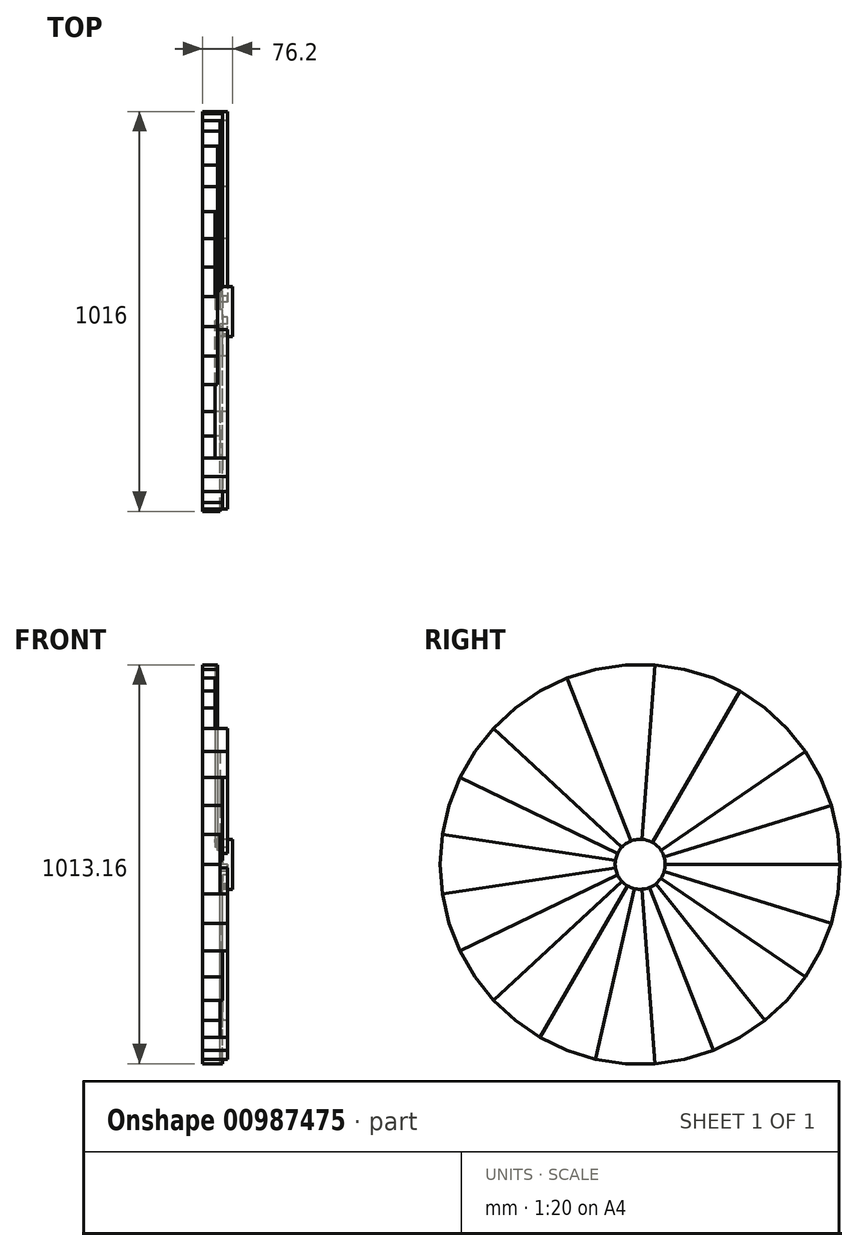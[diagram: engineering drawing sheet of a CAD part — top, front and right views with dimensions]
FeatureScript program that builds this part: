
annotation { "Feature Type Name" : "Feature", "Feature Type Description" : "" }
export const myFeature = defineFeature(function(context is Context, id is Id, definition is map)
    precondition{}
    {
        {
            var Q0;
            Q0=qCreatedBy(makeId("Right.planeOp"),FACE);
            var sketch = newSketch(context, id + "F0", { "sketchPlane" : qUnion([Q0])});
            skCircle(sketch, "E0", {"center": v(0, 0) * mm, "radius": 508 * mm});
            skCircle(sketch, "E1.cCircle", {"center": v(0, 0) * mm, "radius": 508 * mm, "construction": true});
            skLineSegment(sketch, "E1.0", {"start": v(-185.6, 472.88) * mm, "end": v(-113.04, 495.26) * mm});
            skLineSegment(sketch, "E1.1", {"start": v(-113.04, 495.26) * mm, "end": v(-37.96, 506.58) * mm});
            skLineSegment(sketch, "E1.2", {"start": v(-37.96, 506.58) * mm, "end": v(37.96, 506.58) * mm});
            skLineSegment(sketch, "E1.3", {"start": v(37.96, 506.58) * mm, "end": v(113.04, 495.26) * mm});
            skLineSegment(sketch, "E1.4", {"start": v(113.04, 495.26) * mm, "end": v(185.6, 472.88) * mm});
            skLineSegment(sketch, "E1.5", {"start": v(185.6, 472.88) * mm, "end": v(254, 439.94) * mm});
            skLineSegment(sketch, "E1.6", {"start": v(254, 439.94) * mm, "end": v(316.73, 397.17) * mm});
            skLineSegment(sketch, "E1.7", {"start": v(316.73, 397.17) * mm, "end": v(372.4, 345.53) * mm});
            skLineSegment(sketch, "E1.8", {"start": v(372.4, 345.53) * mm, "end": v(419.73, 286.17) * mm});
            skLineSegment(sketch, "E1.9", {"start": v(419.73, 286.17) * mm, "end": v(457.7, 220.41) * mm});
            skLineSegment(sketch, "E1.10", {"start": v(457.7, 220.41) * mm, "end": v(485.43, 149.74) * mm});
            skLineSegment(sketch, "E1.11", {"start": v(485.43, 149.74) * mm, "end": v(502.33, 75.71) * mm});
            skLineSegment(sketch, "E1.12", {"start": v(502.33, 75.71) * mm, "end": v(508, 0) * mm});
            skLineSegment(sketch, "E1.13", {"start": v(508, 0) * mm, "end": v(502.33, -75.71) * mm});
            skLineSegment(sketch, "E1.14", {"start": v(502.33, -75.71) * mm, "end": v(485.43, -149.74) * mm});
            skLineSegment(sketch, "E1.15", {"start": v(485.43, -149.74) * mm, "end": v(457.7, -220.41) * mm});
            skLineSegment(sketch, "E1.16", {"start": v(457.7, -220.41) * mm, "end": v(419.73, -286.17) * mm});
            skLineSegment(sketch, "E1.17", {"start": v(419.73, -286.17) * mm, "end": v(372.4, -345.53) * mm});
            skLineSegment(sketch, "E1.18", {"start": v(372.4, -345.53) * mm, "end": v(316.73, -397.17) * mm});
            skLineSegment(sketch, "E1.19", {"start": v(316.73, -397.17) * mm, "end": v(254, -439.94) * mm});
            skLineSegment(sketch, "E1.20", {"start": v(254, -439.94) * mm, "end": v(185.6, -472.88) * mm});
            skLineSegment(sketch, "E1.21", {"start": v(185.6, -472.88) * mm, "end": v(113.04, -495.26) * mm});
            skLineSegment(sketch, "E1.22", {"start": v(113.04, -495.26) * mm, "end": v(37.96, -506.58) * mm});
            skLineSegment(sketch, "E1.23", {"start": v(37.96, -506.58) * mm, "end": v(-37.96, -506.58) * mm});
            skLineSegment(sketch, "E1.24", {"start": v(-37.96, -506.58) * mm, "end": v(-113.04, -495.26) * mm});
            skLineSegment(sketch, "E1.25", {"start": v(-113.04, -495.26) * mm, "end": v(-185.6, -472.88) * mm});
            skLineSegment(sketch, "E1.26", {"start": v(-185.6, -472.88) * mm, "end": v(-254, -439.94) * mm});
            skLineSegment(sketch, "E1.27", {"start": v(-254, -439.94) * mm, "end": v(-316.73, -397.17) * mm});
            skLineSegment(sketch, "E1.28", {"start": v(-316.73, -397.17) * mm, "end": v(-372.4, -345.53) * mm});
            skLineSegment(sketch, "E1.29", {"start": v(-372.4, -345.53) * mm, "end": v(-419.73, -286.17) * mm});
            skLineSegment(sketch, "E1.30", {"start": v(-419.73, -286.17) * mm, "end": v(-457.7, -220.41) * mm});
            skLineSegment(sketch, "E1.31", {"start": v(-457.7, -220.41) * mm, "end": v(-485.43, -149.74) * mm});
            skLineSegment(sketch, "E1.32", {"start": v(-485.43, -149.74) * mm, "end": v(-502.33, -75.71) * mm});
            skLineSegment(sketch, "E1.33", {"start": v(-502.33, -75.71) * mm, "end": v(-508, 0) * mm});
            skLineSegment(sketch, "E1.34", {"start": v(-508, 0) * mm, "end": v(-502.33, 75.71) * mm});
            skLineSegment(sketch, "E1.35", {"start": v(-502.33, 75.71) * mm, "end": v(-485.43, 149.74) * mm});
            skLineSegment(sketch, "E1.36", {"start": v(-485.43, 149.74) * mm, "end": v(-457.7, 220.41) * mm});
            skLineSegment(sketch, "E1.37", {"start": v(-457.7, 220.41) * mm, "end": v(-419.73, 286.17) * mm});
            skLineSegment(sketch, "E1.38", {"start": v(-419.73, 286.17) * mm, "end": v(-372.4, 345.53) * mm});
            skLineSegment(sketch, "E1.39", {"start": v(-372.4, 345.53) * mm, "end": v(-316.73, 397.17) * mm});
            skLineSegment(sketch, "E1.40", {"start": v(-316.73, 397.17) * mm, "end": v(-254, 439.94) * mm});
            skLineSegment(sketch, "E1.41", {"start": v(-254, 439.94) * mm, "end": v(-185.6, 472.88) * mm});
            skLineSegment(sketch, "E2", {"start": v(37.96, 506.58) * mm, "end": v(0, 0) * mm});
            skLineSegment(sketch, "E3", {"start": v(254, 439.94) * mm, "end": v(0, 0) * mm});
            skLineSegment(sketch, "E4", {"start": v(419.73, 286.17) * mm, "end": v(0, 0) * mm});
            skLineSegment(sketch, "E5", {"start": v(-185.6, 472.88) * mm, "end": v(0, 0) * mm});
            skLineSegment(sketch, "E6", {"start": v(-372.4, 345.53) * mm, "end": v(0, 0) * mm});
            skLineSegment(sketch, "E7", {"start": v(485.43, 149.74) * mm, "end": v(0, 0) * mm});
            skLineSegment(sketch, "E8", {"start": v(508, 0) * mm, "end": v(0, 0) * mm});
            skLineSegment(sketch, "E9", {"start": v(485.43, -149.74) * mm, "end": v(0, 0) * mm});
            skLineSegment(sketch, "E10", {"start": v(419.73, -286.17) * mm, "end": v(0, 0) * mm});
            skLineSegment(sketch, "E11", {"start": v(316.73, -397.17) * mm, "end": v(0, 0) * mm});
            skLineSegment(sketch, "E12", {"start": v(185.6, -472.88) * mm, "end": v(0, 0) * mm});
            skLineSegment(sketch, "E13", {"start": v(37.96, -506.58) * mm, "end": v(0, 0) * mm});
            skLineSegment(sketch, "E14", {"start": v(-113.04, -495.26) * mm, "end": v(0, 0) * mm});
            skLineSegment(sketch, "E15", {"start": v(-254, -439.94) * mm, "end": v(0, 0) * mm});
            skLineSegment(sketch, "E16", {"start": v(-372.4, -345.53) * mm, "end": v(0, 0) * mm});
            skLineSegment(sketch, "E17", {"start": v(-457.7, -220.41) * mm, "end": v(0, 0) * mm});
            skLineSegment(sketch, "E18", {"start": v(-502.33, -75.71) * mm, "end": v(0, 0) * mm});
            skLineSegment(sketch, "E19", {"start": v(-502.33, 75.71) * mm, "end": v(0, 0) * mm});
            skLineSegment(sketch, "E20", {"start": v(-457.7, 220.41) * mm, "end": v(0, 0) * mm});
            skCircle(sketch, "E21", {"center": v(1271.03, -28.32) * mm, "radius": 508 * mm});
            skCircle(sketch, "E22", {"center": v(-1617.24, 20.06) * mm, "radius": 508 * mm});
            skCircle(sketch, "E23.cCircle", {"center": v(-1617.24, 20.06) * mm, "radius": 508 * mm, "construction": true});
            skLineSegment(sketch, "E23.0", {"start": v(-1897.2, 443.96) * mm, "end": v(-1830.9, 480.95) * mm});
            skLineSegment(sketch, "E23.1", {"start": v(-1830.9, 480.95) * mm, "end": v(-1759.81, 507.65) * mm});
            skLineSegment(sketch, "E23.2", {"start": v(-1759.81, 507.65) * mm, "end": v(-1685.55, 523.45) * mm});
            skLineSegment(sketch, "E23.3", {"start": v(-1685.55, 523.45) * mm, "end": v(-1609.76, 528) * mm});
            skLineSegment(sketch, "E23.4", {"start": v(-1609.76, 528) * mm, "end": v(-1534.14, 521.22) * mm});
            skLineSegment(sketch, "E23.5", {"start": v(-1534.14, 521.22) * mm, "end": v(-1460.37, 503.23) * mm});
            skLineSegment(sketch, "E23.6", {"start": v(-1460.37, 503.23) * mm, "end": v(-1390.11, 474.46) * mm});
            skLineSegment(sketch, "E23.7", {"start": v(-1390.11, 474.46) * mm, "end": v(-1324.93, 435.53) * mm});
            skLineSegment(sketch, "E23.8", {"start": v(-1324.93, 435.53) * mm, "end": v(-1266.27, 387.32) * mm});
            skLineSegment(sketch, "E23.9", {"start": v(-1266.27, 387.32) * mm, "end": v(-1215.45, 330.9) * mm});
            skLineSegment(sketch, "E23.10", {"start": v(-1215.45, 330.9) * mm, "end": v(-1173.6, 267.55) * mm});
            skLineSegment(sketch, "E23.11", {"start": v(-1173.6, 267.55) * mm, "end": v(-1141.68, 198.67) * mm});
            skLineSegment(sketch, "E23.12", {"start": v(-1141.68, 198.67) * mm, "end": v(-1120.37, 125.8) * mm});
            skLineSegment(sketch, "E23.13", {"start": v(-1120.37, 125.8) * mm, "end": v(-1110.16, 50.56) * mm});
            skLineSegment(sketch, "E23.14", {"start": v(-1110.16, 50.56) * mm, "end": v(-1111.28, -25.36) * mm});
            skLineSegment(sketch, "E23.15", {"start": v(-1111.28, -25.36) * mm, "end": v(-1123.7, -100.26) * mm});
            skLineSegment(sketch, "E23.16", {"start": v(-1123.7, -100.26) * mm, "end": v(-1147.15, -172.48) * mm});
            skLineSegment(sketch, "E23.17", {"start": v(-1147.15, -172.48) * mm, "end": v(-1181.1, -240.4) * mm});
            skLineSegment(sketch, "E23.18", {"start": v(-1181.1, -240.4) * mm, "end": v(-1224.78, -302.49) * mm});
            skLineSegment(sketch, "E23.19", {"start": v(-1224.78, -302.49) * mm, "end": v(-1277.24, -357.38) * mm});
            skLineSegment(sketch, "E23.20", {"start": v(-1277.24, -357.38) * mm, "end": v(-1337.3, -403.84) * mm});
            skLineSegment(sketch, "E23.21", {"start": v(-1337.3, -403.84) * mm, "end": v(-1403.6, -440.83) * mm});
            skLineSegment(sketch, "E23.22", {"start": v(-1403.6, -440.83) * mm, "end": v(-1474.68, -467.52) * mm});
            skLineSegment(sketch, "E23.23", {"start": v(-1474.68, -467.52) * mm, "end": v(-1548.94, -483.33) * mm});
            skLineSegment(sketch, "E23.24", {"start": v(-1548.94, -483.33) * mm, "end": v(-1624.73, -487.88) * mm});
            skLineSegment(sketch, "E23.25", {"start": v(-1624.73, -487.88) * mm, "end": v(-1700.35, -481.1) * mm});
            skLineSegment(sketch, "E23.26", {"start": v(-1700.35, -481.1) * mm, "end": v(-1774.11, -463.11) * mm});
            skLineSegment(sketch, "E23.27", {"start": v(-1774.11, -463.11) * mm, "end": v(-1844.38, -434.33) * mm});
            skLineSegment(sketch, "E23.28", {"start": v(-1844.38, -434.33) * mm, "end": v(-1909.56, -395.4) * mm});
            skLineSegment(sketch, "E23.29", {"start": v(-1909.56, -395.4) * mm, "end": v(-1968.22, -347.2) * mm});
            skLineSegment(sketch, "E23.30", {"start": v(-1968.22, -347.2) * mm, "end": v(-2019.04, -290.79) * mm});
            skLineSegment(sketch, "E23.31", {"start": v(-2019.04, -290.79) * mm, "end": v(-2060.88, -227.43) * mm});
            skLineSegment(sketch, "E23.32", {"start": v(-2060.88, -227.43) * mm, "end": v(-2092.81, -158.55) * mm});
            skLineSegment(sketch, "E23.33", {"start": v(-2092.81, -158.55) * mm, "end": v(-2114.12, -85.67) * mm});
            skLineSegment(sketch, "E23.34", {"start": v(-2114.12, -85.67) * mm, "end": v(-2124.33, -10.43) * mm});
            skLineSegment(sketch, "E23.35", {"start": v(-2124.33, -10.43) * mm, "end": v(-2123.2, 65.48) * mm});
            skLineSegment(sketch, "E23.36", {"start": v(-2123.2, 65.48) * mm, "end": v(-2110.79, 140.39) * mm});
            skLineSegment(sketch, "E23.37", {"start": v(-2110.79, 140.39) * mm, "end": v(-2087.34, 212.6) * mm});
            skLineSegment(sketch, "E23.38", {"start": v(-2087.34, 212.6) * mm, "end": v(-2053.4, 280.51) * mm});
            skLineSegment(sketch, "E23.39", {"start": v(-2053.4, 280.51) * mm, "end": v(-2009.7, 342.61) * mm});
            skLineSegment(sketch, "E23.40", {"start": v(-2009.7, 342.61) * mm, "end": v(-1957.25, 397.5) * mm});
            skLineSegment(sketch, "E23.41", {"start": v(-1957.25, 397.5) * mm, "end": v(-1897.2, 443.96) * mm});
            skLineSegment(sketch, "E24", {"start": v(-1685.55, 523.45) * mm, "end": v(-1617.24, 20.06) * mm});
            skLineSegment(sketch, "E25", {"start": v(-1460.37, 503.23) * mm, "end": v(-1617.24, 20.06) * mm});
            skLineSegment(sketch, "E26", {"start": v(-1266.27, 387.32) * mm, "end": v(-1617.24, 20.06) * mm});
            skLineSegment(sketch, "E27", {"start": v(-1897.2, 443.96) * mm, "end": v(-1617.24, 20.06) * mm});
            skLineSegment(sketch, "E28", {"start": v(-2053.4, 280.51) * mm, "end": v(-1617.24, 20.06) * mm});
            skLineSegment(sketch, "E29", {"start": v(-1173.6, 267.55) * mm, "end": v(-1617.24, 20.06) * mm});
            skLineSegment(sketch, "E30", {"start": v(-1120.37, 125.8) * mm, "end": v(-1617.24, 20.06) * mm});
            skLineSegment(sketch, "E31", {"start": v(-1111.28, -25.36) * mm, "end": v(-1617.24, 20.06) * mm});
            skLineSegment(sketch, "E32", {"start": v(-1147.15, -172.48) * mm, "end": v(-1617.24, 20.06) * mm});
            skLineSegment(sketch, "E33", {"start": v(-1224.78, -302.49) * mm, "end": v(-1617.24, 20.06) * mm});
            skLineSegment(sketch, "E34", {"start": v(-1337.3, -403.84) * mm, "end": v(-1617.24, 20.06) * mm});
            skLineSegment(sketch, "E35", {"start": v(-1474.68, -467.52) * mm, "end": v(-1617.24, 20.06) * mm});
            skLineSegment(sketch, "E36", {"start": v(-1624.73, -487.88) * mm, "end": v(-1617.24, 20.06) * mm});
            skLineSegment(sketch, "E37", {"start": v(-1774.11, -463.11) * mm, "end": v(-1617.24, 20.06) * mm});
            skLineSegment(sketch, "E38", {"start": v(-1909.56, -395.4) * mm, "end": v(-1617.24, 20.06) * mm});
            skLineSegment(sketch, "E39", {"start": v(-2019.04, -290.79) * mm, "end": v(-1617.24, 20.06) * mm});
            skLineSegment(sketch, "E40", {"start": v(-2092.81, -158.55) * mm, "end": v(-1617.24, 20.06) * mm});
            skLineSegment(sketch, "E41", {"start": v(-2124.33, -10.43) * mm, "end": v(-1617.24, 20.06) * mm});
            skLineSegment(sketch, "E42", {"start": v(-2110.79, 140.39) * mm, "end": v(-1617.24, 20.06) * mm});
            skCircle(sketch, "E43", {"center": v(0, 0) * mm, "radius": 63.5 * mm});
            skLineSegment(sketch, "E44", {"start": v(0, 0) * mm, "end": v(0, 508) * mm, "construction": true});
            skSolve(sketch);
        }
        {
            var Q0;
            Q0=makeQuery(id+"F0.imprint","IMPRINT",FACE,{"disambiguationData":[TD([[makeQuery(id+"F0.imprint","IMPRINT",EDGE,{"derivedFrom":sQuery(id+"F0.wireOp",EDGE,"E1.0")}),-1.0]])]});
            var Q1;
            Q1=makeQuery(id+"F0.imprint","IMPRINT",FACE,{"disambiguationData":[TD([[makeQuery(id+"F0.imprint","IMPRINT",EDGE,{"derivedFrom":sQuery(id+"F0.wireOp",EDGE,"E1.3")}),-1.0]])]});
            var Q2;
            Q2=makeQuery(id+"F0.imprint","IMPRINT",FACE,{"disambiguationData":[TD([[makeQuery(id+"F0.imprint","IMPRINT",EDGE,{"derivedFrom":sQuery(id+"F0.wireOp",EDGE,"E1.6")}),-1.0]])]});
            var Q3;
            Q3=makeQuery(id+"F0.imprint","IMPRINT",FACE,{"disambiguationData":[TD([[makeQuery(id+"F0.imprint","IMPRINT",EDGE,{"derivedFrom":sQuery(id+"F0.wireOp",EDGE,"E1.9")}),-1.0]])]});
            var Q4;
            Q4=makeQuery(id+"F0.imprint","IMPRINT",FACE,{"disambiguationData":[TD([[makeQuery(id+"F0.imprint","IMPRINT",EDGE,{"derivedFrom":sQuery(id+"F0.wireOp",EDGE,"E1.11")}),-1.0]])]});
            var Q5;
            Q5=makeQuery(id+"F0.imprint","IMPRINT",FACE,{"disambiguationData":[TD([[makeQuery(id+"F0.imprint","IMPRINT",EDGE,{"derivedFrom":sQuery(id+"F0.wireOp",EDGE,"E1.13")}),-1.0]])]});
            var Q6;
            Q6=makeQuery(id+"F0.imprint","IMPRINT",FACE,{"disambiguationData":[TD([[makeQuery(id+"F0.imprint","IMPRINT",EDGE,{"derivedFrom":sQuery(id+"F0.wireOp",EDGE,"E1.15")}),-1.0]])]});
            var Q7;
            Q7=makeQuery(id+"F0.imprint","IMPRINT",FACE,{"disambiguationData":[TD([[makeQuery(id+"F0.imprint","IMPRINT",EDGE,{"derivedFrom":sQuery(id+"F0.wireOp",EDGE,"E1.17")}),-1.0]])]});
            var Q8;
            Q8=makeQuery(id+"F0.imprint","IMPRINT",FACE,{"disambiguationData":[TD([[makeQuery(id+"F0.imprint","IMPRINT",EDGE,{"derivedFrom":sQuery(id+"F0.wireOp",EDGE,"E1.19")}),-1.0]])]});
            var Q9;
            Q9=makeQuery(id+"F0.imprint","IMPRINT",FACE,{"disambiguationData":[TD([[makeQuery(id+"F0.imprint","IMPRINT",EDGE,{"derivedFrom":sQuery(id+"F0.wireOp",EDGE,"E1.21")}),-1.0]])]});
            var Q10;
            Q10=makeQuery(id+"F0.imprint","IMPRINT",FACE,{"disambiguationData":[TD([[makeQuery(id+"F0.imprint","IMPRINT",EDGE,{"derivedFrom":sQuery(id+"F0.wireOp",EDGE,"E1.23")}),-1.0]])]});
            var Q11;
            Q11=makeQuery(id+"F0.imprint","IMPRINT",FACE,{"disambiguationData":[TD([[makeQuery(id+"F0.imprint","IMPRINT",EDGE,{"derivedFrom":sQuery(id+"F0.wireOp",EDGE,"E1.25")}),-1.0]])]});
            var Q12;
            Q12=makeQuery(id+"F0.imprint","IMPRINT",FACE,{"disambiguationData":[TD([[makeQuery(id+"F0.imprint","IMPRINT",EDGE,{"derivedFrom":sQuery(id+"F0.wireOp",EDGE,"E1.27")}),-1.0]])]});
            var Q13;
            Q13=makeQuery(id+"F0.imprint","IMPRINT",FACE,{"disambiguationData":[TD([[makeQuery(id+"F0.imprint","IMPRINT",EDGE,{"derivedFrom":sQuery(id+"F0.wireOp",EDGE,"E1.29")}),-1.0]])]});
            var Q14;
            Q14=makeQuery(id+"F0.imprint","IMPRINT",FACE,{"disambiguationData":[TD([[makeQuery(id+"F0.imprint","IMPRINT",EDGE,{"derivedFrom":sQuery(id+"F0.wireOp",EDGE,"E1.31")}),-1.0]])]});
            var Q15;
            Q15=makeQuery(id+"F0.imprint","IMPRINT",FACE,{"disambiguationData":[TD([[makeQuery(id+"F0.imprint","IMPRINT",EDGE,{"derivedFrom":sQuery(id+"F0.wireOp",EDGE,"E1.33")}),-1.0]])]});
            var Q16;
            Q16=makeQuery(id+"F0.imprint","IMPRINT",FACE,{"disambiguationData":[TD([[makeQuery(id+"F0.imprint","IMPRINT",EDGE,{"derivedFrom":sQuery(id+"F0.wireOp",EDGE,"E1.35")}),-1.0]])]});
            var Q17;
            Q17=makeQuery(id+"F0.imprint","IMPRINT",FACE,{"disambiguationData":[TD([[makeQuery(id+"F0.imprint","IMPRINT",EDGE,{"derivedFrom":sQuery(id+"F0.wireOp",EDGE,"E1.37")}),-1.0]])]});
            var Q18;
            Q18=makeQuery(id+"F0.imprint","IMPRINT",FACE,{"disambiguationData":[TD([[makeQuery(id+"F0.imprint","IMPRINT",EDGE,{"derivedFrom":sQuery(id+"F0.wireOp",EDGE,"E1.39")}),-1.0]])]});
            extrude(context, id + "F1", {"entities" : qUnion([Q0, Q1, Q2, Q3, Q4, Q5, Q6, Q7, Q8, Q9, Q10, Q11, Q12, Q13, Q14, Q15, Q16, Q17, Q18]), "depth" : 25.4 * mm, "offsetDistance" : 25.4 * mm});
        }
        {
            var Q0;
            {var subQ1=sQuery(id+"F0.wireOp",EDGE,"E1.3");Q0=makeQuery(id+"F0.imprint","IMPRINT",FACE,{"disambiguationData":[TD([[makeQuery(id+"F0.imprint","IMPRINT",EDGE,{"derivedFrom":subQ1}),-1.0]])]});}
            var Q1;
            {var subQ5=sQuery(id+"F0.wireOp",EDGE,"E1.39");Q1=makeQuery(id+"F0.imprint","IMPRINT",FACE,{"disambiguationData":[TD([[makeQuery(id+"F0.imprint","IMPRINT",EDGE,{"derivedFrom":subQ5}),-1.0]])]});}
            var Q2;
            {var subQ1=sQuery(id+"F0.wireOp",EDGE,"E2");var subQ3=sQuery(id+"F0.wireOp",EDGE,"E43");var subQ4=makeQuery(id+"F0.imprint","INTERSECT",VERTEX,{"derivedFrom":[subQ1,subQ3]});Q2=makeQuery(id+"F0.imprint","IMPRINT",FACE,{"disambiguationData":[TD([[makeQuery(id+"F0.imprint","IMPRINT",EDGE,{"disambiguationData":[TD([[subQ4,1.0]])],"derivedFrom":subQ3}),1.0]])]});}
            var Q3;
            {var subQ1=sQuery(id+"F0.wireOp",EDGE,"E2");var subQ3=sQuery(id+"F0.wireOp",EDGE,"E43");var subQ4=makeQuery(id+"F0.imprint","INTERSECT",VERTEX,{"derivedFrom":[subQ1,subQ3]});Q3=makeQuery(id+"F0.imprint","IMPRINT",FACE,{"disambiguationData":[TD([[makeQuery(id+"F0.imprint","IMPRINT",EDGE,{"disambiguationData":[TD([[subQ4,-1.0]])],"derivedFrom":subQ3}),1.0]])]});}
            var Q4;
            {var subQ1=sQuery(id+"F0.wireOp",EDGE,"E5");var subQ3=sQuery(id+"F0.wireOp",EDGE,"E43");var subQ4=makeQuery(id+"F0.imprint","INTERSECT",VERTEX,{"derivedFrom":[subQ1,subQ3]});Q4=makeQuery(id+"F0.imprint","IMPRINT",FACE,{"disambiguationData":[TD([[makeQuery(id+"F0.imprint","IMPRINT",EDGE,{"disambiguationData":[TD([[subQ4,-1.0]])],"derivedFrom":subQ3}),1.0]])]});}
            extrude(context, id + "F2", {"entities" : qUnion([Q0, Q1, Q2, Q3, Q4]), "operationType" : NewBodyOperationType.ADD, "depth" : 31.75 * mm, "offsetDistance" : 25.4 * mm});
        }
        {
            var Q0;
            {var subQ7=sQuery(id+"F0.wireOp",EDGE,"E1.0");Q0=makeQuery(id+"F0.imprint","IMPRINT",FACE,{"disambiguationData":[TD([[makeQuery(id+"F0.imprint","IMPRINT",EDGE,{"derivedFrom":subQ7}),-1.0]])]});}
            var Q1;
            {var subQ1=sQuery(id+"F0.wireOp",EDGE,"E1.6");Q1=makeQuery(id+"F0.imprint","IMPRINT",FACE,{"disambiguationData":[TD([[makeQuery(id+"F0.imprint","IMPRINT",EDGE,{"derivedFrom":subQ1}),-1.0]])]});}
            var Q2;
            {var subQ1=sQuery(id+"F0.wireOp",EDGE,"E3");var subQ3=sQuery(id+"F0.wireOp",EDGE,"E43");var subQ4=makeQuery(id+"F0.imprint","INTERSECT",VERTEX,{"derivedFrom":[subQ1,subQ3]});Q2=makeQuery(id+"F0.imprint","IMPRINT",FACE,{"disambiguationData":[TD([[makeQuery(id+"F0.imprint","IMPRINT",EDGE,{"disambiguationData":[TD([[subQ4,1.0]])],"derivedFrom":subQ3}),1.0]])]});}
            var Q3;
            {var subQ1=sQuery(id+"F0.wireOp",EDGE,"E2");var subQ3=sQuery(id+"F0.wireOp",EDGE,"E43");var subQ4=makeQuery(id+"F0.imprint","INTERSECT",VERTEX,{"derivedFrom":[subQ1,subQ3]});Q3=makeQuery(id+"F0.imprint","IMPRINT",FACE,{"disambiguationData":[TD([[makeQuery(id+"F0.imprint","IMPRINT",EDGE,{"disambiguationData":[TD([[subQ4,1.0]])],"derivedFrom":subQ3}),1.0]])]});}
            var Q4;
            {var subQ1=sQuery(id+"F0.wireOp",EDGE,"E2");var subQ3=sQuery(id+"F0.wireOp",EDGE,"E43");var subQ4=makeQuery(id+"F0.imprint","INTERSECT",VERTEX,{"derivedFrom":[subQ1,subQ3]});Q4=makeQuery(id+"F0.imprint","IMPRINT",FACE,{"disambiguationData":[TD([[makeQuery(id+"F0.imprint","IMPRINT",EDGE,{"disambiguationData":[TD([[subQ4,-1.0]])],"derivedFrom":subQ3}),1.0]])]});}
            extrude(context, id + "F3", {"entities" : qUnion([Q0, Q1, Q2, Q3, Q4]), "operationType" : NewBodyOperationType.ADD, "depth" : 38.1 * mm, "offsetDistance" : 25.4 * mm});
        }
        {
            var Q0;
            {var subQ6=sQuery(id+"F0.wireOp",EDGE,"E1.9");Q0=makeQuery(id+"F0.imprint","IMPRINT",FACE,{"disambiguationData":[TD([[makeQuery(id+"F0.imprint","IMPRINT",EDGE,{"derivedFrom":subQ6}),-1.0]])]});}
            var Q1;
            {var subQ7=sQuery(id+"F0.wireOp",EDGE,"E1.15");Q1=makeQuery(id+"F0.imprint","IMPRINT",FACE,{"disambiguationData":[TD([[makeQuery(id+"F0.imprint","IMPRINT",EDGE,{"derivedFrom":subQ7}),-1.0]])]});}
            var Q2;
            {var subQ6=sQuery(id+"F0.wireOp",EDGE,"E1.21");Q2=makeQuery(id+"F0.imprint","IMPRINT",FACE,{"disambiguationData":[TD([[makeQuery(id+"F0.imprint","IMPRINT",EDGE,{"derivedFrom":subQ6}),-1.0]])]});}
            var Q3;
            {var subQ6=sQuery(id+"F0.wireOp",EDGE,"E1.27");Q3=makeQuery(id+"F0.imprint","IMPRINT",FACE,{"disambiguationData":[TD([[makeQuery(id+"F0.imprint","IMPRINT",EDGE,{"derivedFrom":subQ6}),-1.0]])]});}
            var Q4;
            {var subQ6=sQuery(id+"F0.wireOp",EDGE,"E1.33");Q4=makeQuery(id+"F0.imprint","IMPRINT",FACE,{"disambiguationData":[TD([[makeQuery(id+"F0.imprint","IMPRINT",EDGE,{"derivedFrom":subQ6}),-1.0]])]});}
            var Q5;
            {var subQ1=sQuery(id+"F0.wireOp",EDGE,"E4");var subQ3=sQuery(id+"F0.wireOp",EDGE,"E43");var subQ4=makeQuery(id+"F0.imprint","INTERSECT",VERTEX,{"derivedFrom":[subQ1,subQ3]});Q5=makeQuery(id+"F0.imprint","IMPRINT",FACE,{"disambiguationData":[TD([[makeQuery(id+"F0.imprint","IMPRINT",EDGE,{"disambiguationData":[TD([[subQ4,1.0]])],"derivedFrom":subQ3}),1.0]])]});}
            var Q6;
            {var subQ1=sQuery(id+"F0.wireOp",EDGE,"E7");var subQ3=sQuery(id+"F0.wireOp",EDGE,"E43");var subQ4=makeQuery(id+"F0.imprint","INTERSECT",VERTEX,{"derivedFrom":[subQ1,subQ3]});Q6=makeQuery(id+"F0.imprint","IMPRINT",FACE,{"disambiguationData":[TD([[makeQuery(id+"F0.imprint","IMPRINT",EDGE,{"disambiguationData":[TD([[subQ4,1.0]])],"derivedFrom":subQ3}),1.0]])]});}
            var Q7;
            {var subQ1=sQuery(id+"F0.wireOp",EDGE,"E8");var subQ3=sQuery(id+"F0.wireOp",EDGE,"E43");var subQ4=makeQuery(id+"F0.imprint","INTERSECT",VERTEX,{"derivedFrom":[subQ1,subQ3]});Q7=makeQuery(id+"F0.imprint","IMPRINT",FACE,{"disambiguationData":[TD([[makeQuery(id+"F0.imprint","IMPRINT",EDGE,{"disambiguationData":[TD([[subQ4,1.0]])],"derivedFrom":subQ3}),1.0]])]});}
            var Q8;
            {var subQ1=sQuery(id+"F0.wireOp",EDGE,"E9");var subQ3=sQuery(id+"F0.wireOp",EDGE,"E43");var subQ4=makeQuery(id+"F0.imprint","INTERSECT",VERTEX,{"derivedFrom":[subQ1,subQ3]});Q8=makeQuery(id+"F0.imprint","IMPRINT",FACE,{"disambiguationData":[TD([[makeQuery(id+"F0.imprint","IMPRINT",EDGE,{"disambiguationData":[TD([[subQ4,1.0]])],"derivedFrom":subQ3}),1.0]])]});}
            var Q9;
            {var subQ1=sQuery(id+"F0.wireOp",EDGE,"E10");var subQ3=sQuery(id+"F0.wireOp",EDGE,"E43");var subQ4=makeQuery(id+"F0.imprint","INTERSECT",VERTEX,{"derivedFrom":[subQ1,subQ3]});Q9=makeQuery(id+"F0.imprint","IMPRINT",FACE,{"disambiguationData":[TD([[makeQuery(id+"F0.imprint","IMPRINT",EDGE,{"disambiguationData":[TD([[subQ4,1.0]])],"derivedFrom":subQ3}),1.0]])]});}
            var Q10;
            {var subQ1=sQuery(id+"F0.wireOp",EDGE,"E11");var subQ3=sQuery(id+"F0.wireOp",EDGE,"E43");var subQ4=makeQuery(id+"F0.imprint","INTERSECT",VERTEX,{"derivedFrom":[subQ1,subQ3]});Q10=makeQuery(id+"F0.imprint","IMPRINT",FACE,{"disambiguationData":[TD([[makeQuery(id+"F0.imprint","IMPRINT",EDGE,{"disambiguationData":[TD([[subQ4,1.0]])],"derivedFrom":subQ3}),1.0]])]});}
            var Q11;
            {var subQ1=sQuery(id+"F0.wireOp",EDGE,"E12");var subQ3=sQuery(id+"F0.wireOp",EDGE,"E43");var subQ4=makeQuery(id+"F0.imprint","INTERSECT",VERTEX,{"derivedFrom":[subQ1,subQ3]});Q11=makeQuery(id+"F0.imprint","IMPRINT",FACE,{"disambiguationData":[TD([[makeQuery(id+"F0.imprint","IMPRINT",EDGE,{"disambiguationData":[TD([[subQ4,1.0]])],"derivedFrom":subQ3}),1.0]])]});}
            var Q12;
            {var subQ1=sQuery(id+"F0.wireOp",EDGE,"E13");var subQ3=sQuery(id+"F0.wireOp",EDGE,"E43");var subQ4=makeQuery(id+"F0.imprint","INTERSECT",VERTEX,{"derivedFrom":[subQ1,subQ3]});Q12=makeQuery(id+"F0.imprint","IMPRINT",FACE,{"disambiguationData":[TD([[makeQuery(id+"F0.imprint","IMPRINT",EDGE,{"disambiguationData":[TD([[subQ4,1.0]])],"derivedFrom":subQ3}),1.0]])]});}
            var Q13;
            {var subQ1=sQuery(id+"F0.wireOp",EDGE,"E14");var subQ3=sQuery(id+"F0.wireOp",EDGE,"E43");var subQ4=makeQuery(id+"F0.imprint","INTERSECT",VERTEX,{"derivedFrom":[subQ1,subQ3]});Q13=makeQuery(id+"F0.imprint","IMPRINT",FACE,{"disambiguationData":[TD([[makeQuery(id+"F0.imprint","IMPRINT",EDGE,{"disambiguationData":[TD([[subQ4,1.0]])],"derivedFrom":subQ3}),1.0]])]});}
            var Q14;
            {var subQ1=sQuery(id+"F0.wireOp",EDGE,"E15");var subQ3=sQuery(id+"F0.wireOp",EDGE,"E43");var subQ4=makeQuery(id+"F0.imprint","INTERSECT",VERTEX,{"derivedFrom":[subQ1,subQ3]});Q14=makeQuery(id+"F0.imprint","IMPRINT",FACE,{"disambiguationData":[TD([[makeQuery(id+"F0.imprint","IMPRINT",EDGE,{"disambiguationData":[TD([[subQ4,1.0]])],"derivedFrom":subQ3}),1.0]])]});}
            var Q15;
            {var subQ1=sQuery(id+"F0.wireOp",EDGE,"E16");var subQ3=sQuery(id+"F0.wireOp",EDGE,"E43");var subQ4=makeQuery(id+"F0.imprint","INTERSECT",VERTEX,{"derivedFrom":[subQ1,subQ3]});Q15=makeQuery(id+"F0.imprint","IMPRINT",FACE,{"disambiguationData":[TD([[makeQuery(id+"F0.imprint","IMPRINT",EDGE,{"disambiguationData":[TD([[subQ4,1.0]])],"derivedFrom":subQ3}),1.0]])]});}
            var Q16;
            {var subQ1=sQuery(id+"F0.wireOp",EDGE,"E17");var subQ3=sQuery(id+"F0.wireOp",EDGE,"E43");var subQ4=makeQuery(id+"F0.imprint","INTERSECT",VERTEX,{"derivedFrom":[subQ1,subQ3]});Q16=makeQuery(id+"F0.imprint","IMPRINT",FACE,{"disambiguationData":[TD([[makeQuery(id+"F0.imprint","IMPRINT",EDGE,{"disambiguationData":[TD([[subQ4,1.0]])],"derivedFrom":subQ3}),1.0]])]});}
            var Q17;
            {var subQ1=sQuery(id+"F0.wireOp",EDGE,"E18");var subQ3=sQuery(id+"F0.wireOp",EDGE,"E43");var subQ4=makeQuery(id+"F0.imprint","INTERSECT",VERTEX,{"derivedFrom":[subQ1,subQ3]});Q17=makeQuery(id+"F0.imprint","IMPRINT",FACE,{"disambiguationData":[TD([[makeQuery(id+"F0.imprint","IMPRINT",EDGE,{"disambiguationData":[TD([[subQ4,1.0]])],"derivedFrom":subQ3}),1.0]])]});}
            extrude(context, id + "F4", {"entities" : qUnion([Q0, Q1, Q2, Q3, Q4, Q5, Q6, Q7, Q8, Q9, Q10, Q11, Q12, Q13, Q14, Q15, Q16, Q17]), "operationType" : NewBodyOperationType.ADD, "depth" : 44.45 * mm, "offsetDistance" : 25.4 * mm});
        }
        {
            var Q0;
            {var subQ6=sQuery(id+"F0.wireOp",EDGE,"E1.11");Q0=makeQuery(id+"F0.imprint","IMPRINT",FACE,{"disambiguationData":[TD([[makeQuery(id+"F0.imprint","IMPRINT",EDGE,{"derivedFrom":subQ6}),-1.0]])]});}
            var Q1;
            {var subQ6=sQuery(id+"F0.wireOp",EDGE,"E1.17");Q1=makeQuery(id+"F0.imprint","IMPRINT",FACE,{"disambiguationData":[TD([[makeQuery(id+"F0.imprint","IMPRINT",EDGE,{"derivedFrom":subQ6}),-1.0]])]});}
            var Q2;
            {var subQ6=sQuery(id+"F0.wireOp",EDGE,"E1.23");Q2=makeQuery(id+"F0.imprint","IMPRINT",FACE,{"disambiguationData":[TD([[makeQuery(id+"F0.imprint","IMPRINT",EDGE,{"derivedFrom":subQ6}),-1.0]])]});}
            var Q3;
            {var subQ6=sQuery(id+"F0.wireOp",EDGE,"E1.29");Q3=makeQuery(id+"F0.imprint","IMPRINT",FACE,{"disambiguationData":[TD([[makeQuery(id+"F0.imprint","IMPRINT",EDGE,{"derivedFrom":subQ6}),-1.0]])]});}
            var Q4;
            {var subQ6=sQuery(id+"F0.wireOp",EDGE,"E1.35");Q4=makeQuery(id+"F0.imprint","IMPRINT",FACE,{"disambiguationData":[TD([[makeQuery(id+"F0.imprint","IMPRINT",EDGE,{"derivedFrom":subQ6}),-1.0]])]});}
            var Q5;
            {var subQ1=sQuery(id+"F0.wireOp",EDGE,"E7");var subQ3=sQuery(id+"F0.wireOp",EDGE,"E43");var subQ4=makeQuery(id+"F0.imprint","INTERSECT",VERTEX,{"derivedFrom":[subQ1,subQ3]});Q5=makeQuery(id+"F0.imprint","IMPRINT",FACE,{"disambiguationData":[TD([[makeQuery(id+"F0.imprint","IMPRINT",EDGE,{"disambiguationData":[TD([[subQ4,1.0]])],"derivedFrom":subQ3}),1.0]])]});}
            var Q6;
            {var subQ1=sQuery(id+"F0.wireOp",EDGE,"E8");var subQ3=sQuery(id+"F0.wireOp",EDGE,"E43");var subQ4=makeQuery(id+"F0.imprint","INTERSECT",VERTEX,{"derivedFrom":[subQ1,subQ3]});Q6=makeQuery(id+"F0.imprint","IMPRINT",FACE,{"disambiguationData":[TD([[makeQuery(id+"F0.imprint","IMPRINT",EDGE,{"disambiguationData":[TD([[subQ4,1.0]])],"derivedFrom":subQ3}),1.0]])]});}
            var Q7;
            {var subQ1=sQuery(id+"F0.wireOp",EDGE,"E9");var subQ3=sQuery(id+"F0.wireOp",EDGE,"E43");var subQ4=makeQuery(id+"F0.imprint","INTERSECT",VERTEX,{"derivedFrom":[subQ1,subQ3]});Q7=makeQuery(id+"F0.imprint","IMPRINT",FACE,{"disambiguationData":[TD([[makeQuery(id+"F0.imprint","IMPRINT",EDGE,{"disambiguationData":[TD([[subQ4,1.0]])],"derivedFrom":subQ3}),1.0]])]});}
            var Q8;
            {var subQ1=sQuery(id+"F0.wireOp",EDGE,"E10");var subQ3=sQuery(id+"F0.wireOp",EDGE,"E43");var subQ4=makeQuery(id+"F0.imprint","INTERSECT",VERTEX,{"derivedFrom":[subQ1,subQ3]});Q8=makeQuery(id+"F0.imprint","IMPRINT",FACE,{"disambiguationData":[TD([[makeQuery(id+"F0.imprint","IMPRINT",EDGE,{"disambiguationData":[TD([[subQ4,1.0]])],"derivedFrom":subQ3}),1.0]])]});}
            var Q9;
            {var subQ1=sQuery(id+"F0.wireOp",EDGE,"E11");var subQ3=sQuery(id+"F0.wireOp",EDGE,"E43");var subQ4=makeQuery(id+"F0.imprint","INTERSECT",VERTEX,{"derivedFrom":[subQ1,subQ3]});Q9=makeQuery(id+"F0.imprint","IMPRINT",FACE,{"disambiguationData":[TD([[makeQuery(id+"F0.imprint","IMPRINT",EDGE,{"disambiguationData":[TD([[subQ4,1.0]])],"derivedFrom":subQ3}),1.0]])]});}
            var Q10;
            {var subQ1=sQuery(id+"F0.wireOp",EDGE,"E12");var subQ3=sQuery(id+"F0.wireOp",EDGE,"E43");var subQ4=makeQuery(id+"F0.imprint","INTERSECT",VERTEX,{"derivedFrom":[subQ1,subQ3]});Q10=makeQuery(id+"F0.imprint","IMPRINT",FACE,{"disambiguationData":[TD([[makeQuery(id+"F0.imprint","IMPRINT",EDGE,{"disambiguationData":[TD([[subQ4,1.0]])],"derivedFrom":subQ3}),1.0]])]});}
            var Q11;
            {var subQ1=sQuery(id+"F0.wireOp",EDGE,"E13");var subQ3=sQuery(id+"F0.wireOp",EDGE,"E43");var subQ4=makeQuery(id+"F0.imprint","INTERSECT",VERTEX,{"derivedFrom":[subQ1,subQ3]});Q11=makeQuery(id+"F0.imprint","IMPRINT",FACE,{"disambiguationData":[TD([[makeQuery(id+"F0.imprint","IMPRINT",EDGE,{"disambiguationData":[TD([[subQ4,1.0]])],"derivedFrom":subQ3}),1.0]])]});}
            var Q12;
            {var subQ1=sQuery(id+"F0.wireOp",EDGE,"E14");var subQ3=sQuery(id+"F0.wireOp",EDGE,"E43");var subQ4=makeQuery(id+"F0.imprint","INTERSECT",VERTEX,{"derivedFrom":[subQ1,subQ3]});Q12=makeQuery(id+"F0.imprint","IMPRINT",FACE,{"disambiguationData":[TD([[makeQuery(id+"F0.imprint","IMPRINT",EDGE,{"disambiguationData":[TD([[subQ4,1.0]])],"derivedFrom":subQ3}),1.0]])]});}
            var Q13;
            {var subQ1=sQuery(id+"F0.wireOp",EDGE,"E15");var subQ3=sQuery(id+"F0.wireOp",EDGE,"E43");var subQ4=makeQuery(id+"F0.imprint","INTERSECT",VERTEX,{"derivedFrom":[subQ1,subQ3]});Q13=makeQuery(id+"F0.imprint","IMPRINT",FACE,{"disambiguationData":[TD([[makeQuery(id+"F0.imprint","IMPRINT",EDGE,{"disambiguationData":[TD([[subQ4,1.0]])],"derivedFrom":subQ3}),1.0]])]});}
            var Q14;
            {var subQ1=sQuery(id+"F0.wireOp",EDGE,"E16");var subQ3=sQuery(id+"F0.wireOp",EDGE,"E43");var subQ4=makeQuery(id+"F0.imprint","INTERSECT",VERTEX,{"derivedFrom":[subQ1,subQ3]});Q14=makeQuery(id+"F0.imprint","IMPRINT",FACE,{"disambiguationData":[TD([[makeQuery(id+"F0.imprint","IMPRINT",EDGE,{"disambiguationData":[TD([[subQ4,1.0]])],"derivedFrom":subQ3}),1.0]])]});}
            var Q15;
            {var subQ1=sQuery(id+"F0.wireOp",EDGE,"E17");var subQ3=sQuery(id+"F0.wireOp",EDGE,"E43");var subQ4=makeQuery(id+"F0.imprint","INTERSECT",VERTEX,{"derivedFrom":[subQ1,subQ3]});Q15=makeQuery(id+"F0.imprint","IMPRINT",FACE,{"disambiguationData":[TD([[makeQuery(id+"F0.imprint","IMPRINT",EDGE,{"disambiguationData":[TD([[subQ4,1.0]])],"derivedFrom":subQ3}),1.0]])]});}
            var Q16;
            {var subQ1=sQuery(id+"F0.wireOp",EDGE,"E18");var subQ3=sQuery(id+"F0.wireOp",EDGE,"E43");var subQ4=makeQuery(id+"F0.imprint","INTERSECT",VERTEX,{"derivedFrom":[subQ1,subQ3]});Q16=makeQuery(id+"F0.imprint","IMPRINT",FACE,{"disambiguationData":[TD([[makeQuery(id+"F0.imprint","IMPRINT",EDGE,{"disambiguationData":[TD([[subQ4,1.0]])],"derivedFrom":subQ3}),1.0]])]});}
            var Q17;
            {var subQ1=sQuery(id+"F0.wireOp",EDGE,"E19");var subQ3=sQuery(id+"F0.wireOp",EDGE,"E43");var subQ4=makeQuery(id+"F0.imprint","INTERSECT",VERTEX,{"derivedFrom":[subQ1,subQ3]});Q17=makeQuery(id+"F0.imprint","IMPRINT",FACE,{"disambiguationData":[TD([[makeQuery(id+"F0.imprint","IMPRINT",EDGE,{"disambiguationData":[TD([[subQ4,1.0]])],"derivedFrom":subQ3}),1.0]])]});}
            extrude(context, id + "F5", {"entities" : qUnion([Q0, Q1, Q2, Q3, Q4, Q5, Q6, Q7, Q8, Q9, Q10, Q11, Q12, Q13, Q14, Q15, Q16, Q17]), "operationType" : NewBodyOperationType.ADD, "depth" : 50.8 * mm, "offsetDistance" : 25.4 * mm});
        }
        {
            var Q0;
            {var subQ6=sQuery(id+"F0.wireOp",EDGE,"E1.13");Q0=makeQuery(id+"F0.imprint","IMPRINT",FACE,{"disambiguationData":[TD([[makeQuery(id+"F0.imprint","IMPRINT",EDGE,{"derivedFrom":subQ6}),-1.0]])]});}
            var Q1;
            {var subQ6=sQuery(id+"F0.wireOp",EDGE,"E1.19");Q1=makeQuery(id+"F0.imprint","IMPRINT",FACE,{"disambiguationData":[TD([[makeQuery(id+"F0.imprint","IMPRINT",EDGE,{"derivedFrom":subQ6}),-1.0]])]});}
            var Q2;
            {var subQ6=sQuery(id+"F0.wireOp",EDGE,"E1.25");Q2=makeQuery(id+"F0.imprint","IMPRINT",FACE,{"disambiguationData":[TD([[makeQuery(id+"F0.imprint","IMPRINT",EDGE,{"derivedFrom":subQ6}),-1.0]])]});}
            var Q3;
            {var subQ6=sQuery(id+"F0.wireOp",EDGE,"E1.31");Q3=makeQuery(id+"F0.imprint","IMPRINT",FACE,{"disambiguationData":[TD([[makeQuery(id+"F0.imprint","IMPRINT",EDGE,{"derivedFrom":subQ6}),-1.0]])]});}
            var Q4;
            {var subQ6=sQuery(id+"F0.wireOp",EDGE,"E1.37");Q4=makeQuery(id+"F0.imprint","IMPRINT",FACE,{"disambiguationData":[TD([[makeQuery(id+"F0.imprint","IMPRINT",EDGE,{"derivedFrom":subQ6}),-1.0]])]});}
            var Q5;
            {var subQ1=sQuery(id+"F0.wireOp",EDGE,"E8");var subQ3=sQuery(id+"F0.wireOp",EDGE,"E43");var subQ4=makeQuery(id+"F0.imprint","INTERSECT",VERTEX,{"derivedFrom":[subQ1,subQ3]});Q5=makeQuery(id+"F0.imprint","IMPRINT",FACE,{"disambiguationData":[TD([[makeQuery(id+"F0.imprint","IMPRINT",EDGE,{"disambiguationData":[TD([[subQ4,1.0]])],"derivedFrom":subQ3}),1.0]])]});}
            var Q6;
            {var subQ1=sQuery(id+"F0.wireOp",EDGE,"E9");var subQ3=sQuery(id+"F0.wireOp",EDGE,"E43");var subQ4=makeQuery(id+"F0.imprint","INTERSECT",VERTEX,{"derivedFrom":[subQ1,subQ3]});Q6=makeQuery(id+"F0.imprint","IMPRINT",FACE,{"disambiguationData":[TD([[makeQuery(id+"F0.imprint","IMPRINT",EDGE,{"disambiguationData":[TD([[subQ4,1.0]])],"derivedFrom":subQ3}),1.0]])]});}
            var Q7;
            {var subQ1=sQuery(id+"F0.wireOp",EDGE,"E10");var subQ3=sQuery(id+"F0.wireOp",EDGE,"E43");var subQ4=makeQuery(id+"F0.imprint","INTERSECT",VERTEX,{"derivedFrom":[subQ1,subQ3]});Q7=makeQuery(id+"F0.imprint","IMPRINT",FACE,{"disambiguationData":[TD([[makeQuery(id+"F0.imprint","IMPRINT",EDGE,{"disambiguationData":[TD([[subQ4,1.0]])],"derivedFrom":subQ3}),1.0]])]});}
            var Q8;
            {var subQ1=sQuery(id+"F0.wireOp",EDGE,"E11");var subQ3=sQuery(id+"F0.wireOp",EDGE,"E43");var subQ4=makeQuery(id+"F0.imprint","INTERSECT",VERTEX,{"derivedFrom":[subQ1,subQ3]});Q8=makeQuery(id+"F0.imprint","IMPRINT",FACE,{"disambiguationData":[TD([[makeQuery(id+"F0.imprint","IMPRINT",EDGE,{"disambiguationData":[TD([[subQ4,1.0]])],"derivedFrom":subQ3}),1.0]])]});}
            var Q9;
            {var subQ1=sQuery(id+"F0.wireOp",EDGE,"E12");var subQ3=sQuery(id+"F0.wireOp",EDGE,"E43");var subQ4=makeQuery(id+"F0.imprint","INTERSECT",VERTEX,{"derivedFrom":[subQ1,subQ3]});Q9=makeQuery(id+"F0.imprint","IMPRINT",FACE,{"disambiguationData":[TD([[makeQuery(id+"F0.imprint","IMPRINT",EDGE,{"disambiguationData":[TD([[subQ4,1.0]])],"derivedFrom":subQ3}),1.0]])]});}
            var Q10;
            {var subQ1=sQuery(id+"F0.wireOp",EDGE,"E13");var subQ3=sQuery(id+"F0.wireOp",EDGE,"E43");var subQ4=makeQuery(id+"F0.imprint","INTERSECT",VERTEX,{"derivedFrom":[subQ1,subQ3]});Q10=makeQuery(id+"F0.imprint","IMPRINT",FACE,{"disambiguationData":[TD([[makeQuery(id+"F0.imprint","IMPRINT",EDGE,{"disambiguationData":[TD([[subQ4,1.0]])],"derivedFrom":subQ3}),1.0]])]});}
            var Q11;
            {var subQ1=sQuery(id+"F0.wireOp",EDGE,"E14");var subQ3=sQuery(id+"F0.wireOp",EDGE,"E43");var subQ4=makeQuery(id+"F0.imprint","INTERSECT",VERTEX,{"derivedFrom":[subQ1,subQ3]});Q11=makeQuery(id+"F0.imprint","IMPRINT",FACE,{"disambiguationData":[TD([[makeQuery(id+"F0.imprint","IMPRINT",EDGE,{"disambiguationData":[TD([[subQ4,1.0]])],"derivedFrom":subQ3}),1.0]])]});}
            var Q12;
            {var subQ1=sQuery(id+"F0.wireOp",EDGE,"E15");var subQ3=sQuery(id+"F0.wireOp",EDGE,"E43");var subQ4=makeQuery(id+"F0.imprint","INTERSECT",VERTEX,{"derivedFrom":[subQ1,subQ3]});Q12=makeQuery(id+"F0.imprint","IMPRINT",FACE,{"disambiguationData":[TD([[makeQuery(id+"F0.imprint","IMPRINT",EDGE,{"disambiguationData":[TD([[subQ4,1.0]])],"derivedFrom":subQ3}),1.0]])]});}
            var Q13;
            {var subQ1=sQuery(id+"F0.wireOp",EDGE,"E16");var subQ3=sQuery(id+"F0.wireOp",EDGE,"E43");var subQ4=makeQuery(id+"F0.imprint","INTERSECT",VERTEX,{"derivedFrom":[subQ1,subQ3]});Q13=makeQuery(id+"F0.imprint","IMPRINT",FACE,{"disambiguationData":[TD([[makeQuery(id+"F0.imprint","IMPRINT",EDGE,{"disambiguationData":[TD([[subQ4,1.0]])],"derivedFrom":subQ3}),1.0]])]});}
            var Q14;
            {var subQ1=sQuery(id+"F0.wireOp",EDGE,"E17");var subQ3=sQuery(id+"F0.wireOp",EDGE,"E43");var subQ4=makeQuery(id+"F0.imprint","INTERSECT",VERTEX,{"derivedFrom":[subQ1,subQ3]});Q14=makeQuery(id+"F0.imprint","IMPRINT",FACE,{"disambiguationData":[TD([[makeQuery(id+"F0.imprint","IMPRINT",EDGE,{"disambiguationData":[TD([[subQ4,1.0]])],"derivedFrom":subQ3}),1.0]])]});}
            var Q15;
            {var subQ1=sQuery(id+"F0.wireOp",EDGE,"E18");var subQ3=sQuery(id+"F0.wireOp",EDGE,"E43");var subQ4=makeQuery(id+"F0.imprint","INTERSECT",VERTEX,{"derivedFrom":[subQ1,subQ3]});Q15=makeQuery(id+"F0.imprint","IMPRINT",FACE,{"disambiguationData":[TD([[makeQuery(id+"F0.imprint","IMPRINT",EDGE,{"disambiguationData":[TD([[subQ4,1.0]])],"derivedFrom":subQ3}),1.0]])]});}
            var Q16;
            {var subQ1=sQuery(id+"F0.wireOp",EDGE,"E19");var subQ3=sQuery(id+"F0.wireOp",EDGE,"E43");var subQ4=makeQuery(id+"F0.imprint","INTERSECT",VERTEX,{"derivedFrom":[subQ1,subQ3]});Q16=makeQuery(id+"F0.imprint","IMPRINT",FACE,{"disambiguationData":[TD([[makeQuery(id+"F0.imprint","IMPRINT",EDGE,{"disambiguationData":[TD([[subQ4,1.0]])],"derivedFrom":subQ3}),1.0]])]});}
            var Q17;
            {var subQ1=sQuery(id+"F0.wireOp",EDGE,"E6");var subQ3=sQuery(id+"F0.wireOp",EDGE,"E43");var subQ4=makeQuery(id+"F0.imprint","INTERSECT",VERTEX,{"derivedFrom":[subQ1,subQ3]});Q17=makeQuery(id+"F0.imprint","IMPRINT",FACE,{"disambiguationData":[TD([[makeQuery(id+"F0.imprint","IMPRINT",EDGE,{"disambiguationData":[TD([[subQ4,-1.0]])],"derivedFrom":subQ3}),1.0]])]});}
            extrude(context, id + "F6", {"entities" : qUnion([Q0, Q1, Q2, Q3, Q4, Q5, Q6, Q7, Q8, Q9, Q10, Q11, Q12, Q13, Q14, Q15, Q16, Q17]), "operationType" : NewBodyOperationType.ADD, "depth" : 63.5 * mm, "offsetDistance" : 25.4 * mm});
        }
        {
            var Q0;
            {var subQ1=sQuery(id+"F0.wireOp",EDGE,"E5");var subQ3=sQuery(id+"F0.wireOp",EDGE,"E43");var subQ4=makeQuery(id+"F0.imprint","INTERSECT",VERTEX,{"derivedFrom":[subQ1,subQ3]});Q0=makeQuery(id+"F0.imprint","IMPRINT",FACE,{"disambiguationData":[TD([[makeQuery(id+"F0.imprint","IMPRINT",EDGE,{"disambiguationData":[TD([[subQ4,-1.0]])],"derivedFrom":subQ3}),1.0]])]});}
            var Q1;
            {var subQ1=sQuery(id+"F0.wireOp",EDGE,"E6");var subQ3=sQuery(id+"F0.wireOp",EDGE,"E43");var subQ4=makeQuery(id+"F0.imprint","INTERSECT",VERTEX,{"derivedFrom":[subQ1,subQ3]});Q1=makeQuery(id+"F0.imprint","IMPRINT",FACE,{"disambiguationData":[TD([[makeQuery(id+"F0.imprint","IMPRINT",EDGE,{"disambiguationData":[TD([[subQ4,-1.0]])],"derivedFrom":subQ3}),1.0]])]});}
            var Q2;
            {var subQ1=sQuery(id+"F0.wireOp",EDGE,"E19");var subQ3=sQuery(id+"F0.wireOp",EDGE,"E43");var subQ4=makeQuery(id+"F0.imprint","INTERSECT",VERTEX,{"derivedFrom":[subQ1,subQ3]});Q2=makeQuery(id+"F0.imprint","IMPRINT",FACE,{"disambiguationData":[TD([[makeQuery(id+"F0.imprint","IMPRINT",EDGE,{"disambiguationData":[TD([[subQ4,1.0]])],"derivedFrom":subQ3}),1.0]])]});}
            var Q3;
            {var subQ1=sQuery(id+"F0.wireOp",EDGE,"E18");var subQ3=sQuery(id+"F0.wireOp",EDGE,"E43");var subQ4=makeQuery(id+"F0.imprint","INTERSECT",VERTEX,{"derivedFrom":[subQ1,subQ3]});Q3=makeQuery(id+"F0.imprint","IMPRINT",FACE,{"disambiguationData":[TD([[makeQuery(id+"F0.imprint","IMPRINT",EDGE,{"disambiguationData":[TD([[subQ4,1.0]])],"derivedFrom":subQ3}),1.0]])]});}
            var Q4;
            {var subQ1=sQuery(id+"F0.wireOp",EDGE,"E17");var subQ3=sQuery(id+"F0.wireOp",EDGE,"E43");var subQ4=makeQuery(id+"F0.imprint","INTERSECT",VERTEX,{"derivedFrom":[subQ1,subQ3]});Q4=makeQuery(id+"F0.imprint","IMPRINT",FACE,{"disambiguationData":[TD([[makeQuery(id+"F0.imprint","IMPRINT",EDGE,{"disambiguationData":[TD([[subQ4,1.0]])],"derivedFrom":subQ3}),1.0]])]});}
            var Q5;
            {var subQ1=sQuery(id+"F0.wireOp",EDGE,"E16");var subQ3=sQuery(id+"F0.wireOp",EDGE,"E43");var subQ4=makeQuery(id+"F0.imprint","INTERSECT",VERTEX,{"derivedFrom":[subQ1,subQ3]});Q5=makeQuery(id+"F0.imprint","IMPRINT",FACE,{"disambiguationData":[TD([[makeQuery(id+"F0.imprint","IMPRINT",EDGE,{"disambiguationData":[TD([[subQ4,1.0]])],"derivedFrom":subQ3}),1.0]])]});}
            var Q6;
            {var subQ1=sQuery(id+"F0.wireOp",EDGE,"E15");var subQ3=sQuery(id+"F0.wireOp",EDGE,"E43");var subQ4=makeQuery(id+"F0.imprint","INTERSECT",VERTEX,{"derivedFrom":[subQ1,subQ3]});Q6=makeQuery(id+"F0.imprint","IMPRINT",FACE,{"disambiguationData":[TD([[makeQuery(id+"F0.imprint","IMPRINT",EDGE,{"disambiguationData":[TD([[subQ4,1.0]])],"derivedFrom":subQ3}),1.0]])]});}
            var Q7;
            {var subQ1=sQuery(id+"F0.wireOp",EDGE,"E14");var subQ3=sQuery(id+"F0.wireOp",EDGE,"E43");var subQ4=makeQuery(id+"F0.imprint","INTERSECT",VERTEX,{"derivedFrom":[subQ1,subQ3]});Q7=makeQuery(id+"F0.imprint","IMPRINT",FACE,{"disambiguationData":[TD([[makeQuery(id+"F0.imprint","IMPRINT",EDGE,{"disambiguationData":[TD([[subQ4,1.0]])],"derivedFrom":subQ3}),1.0]])]});}
            var Q8;
            {var subQ1=sQuery(id+"F0.wireOp",EDGE,"E13");var subQ3=sQuery(id+"F0.wireOp",EDGE,"E43");var subQ4=makeQuery(id+"F0.imprint","INTERSECT",VERTEX,{"derivedFrom":[subQ1,subQ3]});Q8=makeQuery(id+"F0.imprint","IMPRINT",FACE,{"disambiguationData":[TD([[makeQuery(id+"F0.imprint","IMPRINT",EDGE,{"disambiguationData":[TD([[subQ4,1.0]])],"derivedFrom":subQ3}),1.0]])]});}
            var Q9;
            {var subQ1=sQuery(id+"F0.wireOp",EDGE,"E12");var subQ3=sQuery(id+"F0.wireOp",EDGE,"E43");var subQ4=makeQuery(id+"F0.imprint","INTERSECT",VERTEX,{"derivedFrom":[subQ1,subQ3]});Q9=makeQuery(id+"F0.imprint","IMPRINT",FACE,{"disambiguationData":[TD([[makeQuery(id+"F0.imprint","IMPRINT",EDGE,{"disambiguationData":[TD([[subQ4,1.0]])],"derivedFrom":subQ3}),1.0]])]});}
            var Q10;
            {var subQ1=sQuery(id+"F0.wireOp",EDGE,"E11");var subQ3=sQuery(id+"F0.wireOp",EDGE,"E43");var subQ4=makeQuery(id+"F0.imprint","INTERSECT",VERTEX,{"derivedFrom":[subQ1,subQ3]});Q10=makeQuery(id+"F0.imprint","IMPRINT",FACE,{"disambiguationData":[TD([[makeQuery(id+"F0.imprint","IMPRINT",EDGE,{"disambiguationData":[TD([[subQ4,1.0]])],"derivedFrom":subQ3}),1.0]])]});}
            var Q11;
            {var subQ1=sQuery(id+"F0.wireOp",EDGE,"E10");var subQ3=sQuery(id+"F0.wireOp",EDGE,"E43");var subQ4=makeQuery(id+"F0.imprint","INTERSECT",VERTEX,{"derivedFrom":[subQ1,subQ3]});Q11=makeQuery(id+"F0.imprint","IMPRINT",FACE,{"disambiguationData":[TD([[makeQuery(id+"F0.imprint","IMPRINT",EDGE,{"disambiguationData":[TD([[subQ4,1.0]])],"derivedFrom":subQ3}),1.0]])]});}
            var Q12;
            {var subQ1=sQuery(id+"F0.wireOp",EDGE,"E9");var subQ3=sQuery(id+"F0.wireOp",EDGE,"E43");var subQ4=makeQuery(id+"F0.imprint","INTERSECT",VERTEX,{"derivedFrom":[subQ1,subQ3]});Q12=makeQuery(id+"F0.imprint","IMPRINT",FACE,{"disambiguationData":[TD([[makeQuery(id+"F0.imprint","IMPRINT",EDGE,{"disambiguationData":[TD([[subQ4,1.0]])],"derivedFrom":subQ3}),1.0]])]});}
            var Q13;
            {var subQ1=sQuery(id+"F0.wireOp",EDGE,"E8");var subQ3=sQuery(id+"F0.wireOp",EDGE,"E43");var subQ4=makeQuery(id+"F0.imprint","INTERSECT",VERTEX,{"derivedFrom":[subQ1,subQ3]});Q13=makeQuery(id+"F0.imprint","IMPRINT",FACE,{"disambiguationData":[TD([[makeQuery(id+"F0.imprint","IMPRINT",EDGE,{"disambiguationData":[TD([[subQ4,1.0]])],"derivedFrom":subQ3}),1.0]])]});}
            var Q14;
            {var subQ1=sQuery(id+"F0.wireOp",EDGE,"E7");var subQ3=sQuery(id+"F0.wireOp",EDGE,"E43");var subQ4=makeQuery(id+"F0.imprint","INTERSECT",VERTEX,{"derivedFrom":[subQ1,subQ3]});Q14=makeQuery(id+"F0.imprint","IMPRINT",FACE,{"disambiguationData":[TD([[makeQuery(id+"F0.imprint","IMPRINT",EDGE,{"disambiguationData":[TD([[subQ4,1.0]])],"derivedFrom":subQ3}),1.0]])]});}
            var Q15;
            {var subQ1=sQuery(id+"F0.wireOp",EDGE,"E4");var subQ3=sQuery(id+"F0.wireOp",EDGE,"E43");var subQ4=makeQuery(id+"F0.imprint","INTERSECT",VERTEX,{"derivedFrom":[subQ1,subQ3]});Q15=makeQuery(id+"F0.imprint","IMPRINT",FACE,{"disambiguationData":[TD([[makeQuery(id+"F0.imprint","IMPRINT",EDGE,{"disambiguationData":[TD([[subQ4,1.0]])],"derivedFrom":subQ3}),1.0]])]});}
            var Q16;
            {var subQ1=sQuery(id+"F0.wireOp",EDGE,"E3");var subQ3=sQuery(id+"F0.wireOp",EDGE,"E43");var subQ4=makeQuery(id+"F0.imprint","INTERSECT",VERTEX,{"derivedFrom":[subQ1,subQ3]});Q16=makeQuery(id+"F0.imprint","IMPRINT",FACE,{"disambiguationData":[TD([[makeQuery(id+"F0.imprint","IMPRINT",EDGE,{"disambiguationData":[TD([[subQ4,1.0]])],"derivedFrom":subQ3}),1.0]])]});}
            var Q17;
            {var subQ1=sQuery(id+"F0.wireOp",EDGE,"E2");var subQ3=sQuery(id+"F0.wireOp",EDGE,"E43");var subQ4=makeQuery(id+"F0.imprint","INTERSECT",VERTEX,{"derivedFrom":[subQ1,subQ3]});Q17=makeQuery(id+"F0.imprint","IMPRINT",FACE,{"disambiguationData":[TD([[makeQuery(id+"F0.imprint","IMPRINT",EDGE,{"disambiguationData":[TD([[subQ4,1.0]])],"derivedFrom":subQ3}),1.0]])]});}
            var Q18;
            {var subQ1=sQuery(id+"F0.wireOp",EDGE,"E2");var subQ3=sQuery(id+"F0.wireOp",EDGE,"E43");var subQ4=makeQuery(id+"F0.imprint","INTERSECT",VERTEX,{"derivedFrom":[subQ1,subQ3]});Q18=makeQuery(id+"F0.imprint","IMPRINT",FACE,{"disambiguationData":[TD([[makeQuery(id+"F0.imprint","IMPRINT",EDGE,{"disambiguationData":[TD([[subQ4,-1.0]])],"derivedFrom":subQ3}),1.0]])]});}
            extrude(context, id + "F7", {"entities" : qUnion([Q0, Q1, Q2, Q3, Q4, Q5, Q6, Q7, Q8, Q9, Q10, Q11, Q12, Q13, Q14, Q15, Q16, Q17, Q18]), "operationType" : NewBodyOperationType.ADD, "depth" : 76.2 * mm, "offsetDistance" : 25.4 * mm});
        }
    });
